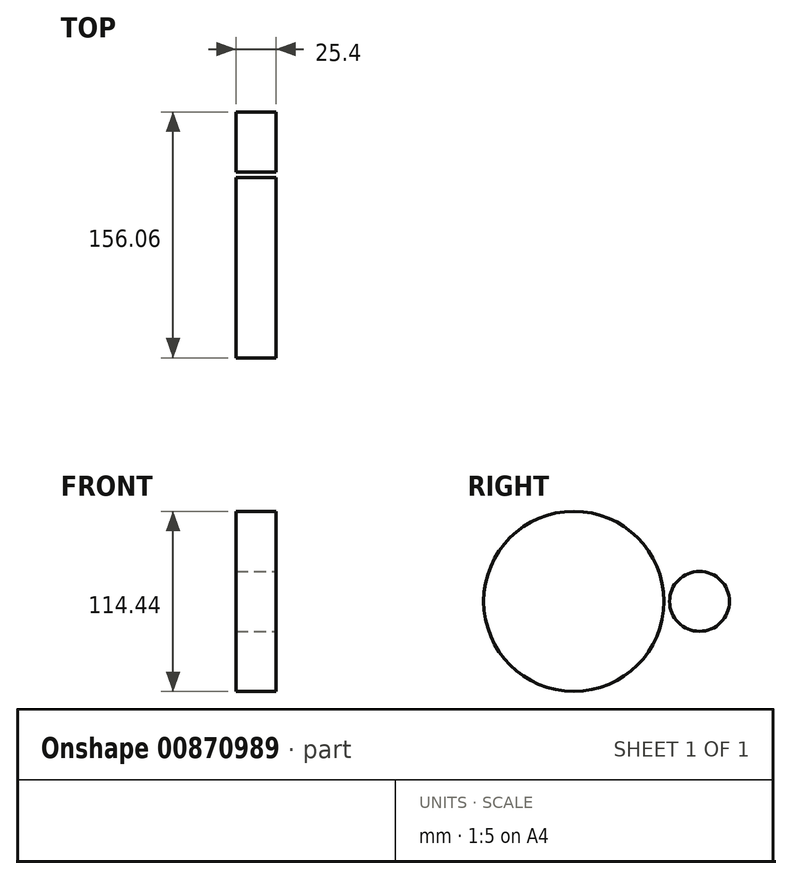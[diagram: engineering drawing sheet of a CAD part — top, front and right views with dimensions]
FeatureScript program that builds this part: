
annotation { "Feature Type Name" : "Feature", "Feature Type Description" : "" }
export const myFeature = defineFeature(function(context is Context, id is Id, definition is map)
    precondition{}
    {
        {
            var Q0;
            Q0=qCreatedBy(makeId("Right.planeOp"),FACE);
            var sketch = newSketch(context, id + "F0", { "sketchPlane" : qUnion([Q0])});
            skCircle(sketch, "E0", {"center": v(0, 0) * mm, "radius": 57.22 * mm});
            skSolve(sketch);
        }
        {
            var Q0;
            Q0=sQuery(id+"F0.wireOp",EDGE,"E0");
            extrude(context, id + "F1", {"bodyType" : ToolBodyType.SURFACE, "surfaceEntities" : qUnion([Q0]), "depth" : 25.4 * mm, "offsetDistance" : 25.4 * mm});
        }
        {
            var Q0;
            Q0=qCreatedBy(makeId("Right.planeOp"),FACE);
            var sketch = newSketch(context, id + "F2", { "sketchPlane" : qUnion([Q0])});
            skCircle(sketch, "E1", {"center": v(79.83, 0) * mm, "radius": 19 * mm});
            skSolve(sketch);
        }
        {
            var Q0;
            Q0=sQuery(id+"F2.wireOp",EDGE,"E1");
            extrude(context, id + "F3", {"bodyType" : ToolBodyType.SURFACE, "surfaceEntities" : qUnion([Q0]), "depth" : 25.4 * mm, "offsetDistance" : 25.4 * mm});
        }
    });
